# Revit family: LEGRAND_ECLAIRAGE_DE_SECURITE_KICKSPOT
name_source: partatom
category: Luminaires
units: mm (PartAtom-declared; Revit-internal decimal feet)

## family parameters
Cote de connecteur circulaire = Utiliser le diamètre
Couper avec des vides une fois chargée = Non
Hôte = Face
Partagée = Non
Point de calcul de pièce = Non
Source d'éclairage = Oui
Type d'élément = Normal

## types (14) — shared parameters
Angle de l'inclinaison = 60.00°
CLASSE_DE_PROTECTION = II
CLASSE_DE_PROTECTION_(IP) = IP40
COULEUR_DU_BOITIER = blanc
Condition Générale d'Utilisation = https://export.legrand.com
DIAMETRE_EXTERNE = 187
DISTANCE_DE_RECONNAISSANCE = 15
DUREE_DE_GARANTIE_BAES_COMPLET = 2
Elévation par défaut = 1219 mm
Emettre à partir de la longueur de la ligne = 610 mm
FORMAT_PRODUIT = rond
Fichier de distribution photométrique = generic
Filtre de couleur = 16777215
Gradation des changements de température de couleur de lampe = <Aucun>
INSTALLATION_DE_SURVEILLANCE = auto-test automatique
LARGEUR = 187
MATERIAU_DU_BOITIER = plastique
MATERIAU_DU_COUVERCLE = plastique transparent
PROFONDEUR_D'ENCASTREMENT = 61.5
SOURCE_LUMINEUSE = LED non interchangeable
SUPPORT_PLAFOND = Oui
TYPE_DE_MONTAGE = encastré

## per-type parameters (varying)
| type | ADAPTE_AU_TYPE_DE_MARQUAGE | ALIMENTATION | CATEGORIE_PRODUIT | DIAMETRE_D'ENCASTREMENT | ETAT_DES_ACCUS | FLUX_LUMINEUX_EN_MODE_D'URGENCE | FONCTION | HAUTEUR/PROFONDEUR | LARGEUR_DE_MONTAGE | LONGUEUR | LONGUEUR_D'ENCASTREMENT | PORTE_PICTO | PUISSANCE_DE_LA_LAMPE | REFERENCE_ARTICLE | REF_BATTERIE_DE_RECHANGE | RESERVE_DE_MARCHE | TENSION_NOMINALE_(MAX) | TENSION_NOMINALE_(MIN) | TYPE_DE_COMMUTATION | TYPE_DE_TENSION |
| BAES+BAEH  KICKSPOT ECO1 AUTOD | feuillet/plaque inséré(e) | décentralisé (batterie individuelle) | Autonome | 152 | NiCd | 45 | BAEH | 202 | 152 | 240 | 152 | Oui | 1 | 062514 | 061087 | 1 | 253 | 207 | mode veille | CA |
| BAES EVAC KICKSPOT ECO1 AUTOD | feuillet/plaque inséré(e) | décentralisé (batterie individuelle) | Autonome | 152 | NiCd | 45 | Evac | 202 | 152 | 240 | 152 | Oui | 0.5 | 062524 | 061087 | 1 | 253 | 207 | mode veille | CA |
| DBR KICKSPOT ECO1 AUTOD | feuillet/plaque inséré(e) | décentralisé (batterie individuelle) | Autonome | 151 | NiCd | 45 | DBR | 202 | 151 | 240 | 151 | Oui | 1 | 062554 | 061087 | 1 | 253 | 207 | mode veille | CA |
| BAES AMB KICKSPOT ECO1 AUTOD |  | décentralisé (batterie individuelle) | Autonome | 152 | NiMh | 320 | Amb | 76 | 152 | 187 | 152 | Non | 4 | 062564 | 061088 | 1 | 253 | 207 | mode veille | CA |
| BAEH KICKSPOT ECO1 AUTOD | feuillet/plaque inséré(e) | décentralisé (batterie individuelle) | Autonome | 152 | NiCd | 8 | BAES+BAEH | 76 | 152 | 187 | 152 | Non | 0.09 | 062574 | 061087 | 5 | 253 | 207 | mode veille | CA |
| BAES+BAEH KICKSPOT ECO2 ADR | feuillet/plaque inséré(e) | décentralisé (batterie individuelle) | Autonome | 152 | NiMh | 45 | BAEH | 202 | 152 | 240 | 152 | Oui | 1 | 062614 | 2*061088 | 1 | 253 | 207 | mode veille | CA |
| BAES EVAC KICKSPOT ECO2 ADR | feuillet/plaque inséré(e) | décentralisé (batterie individuelle) | Autonome | 152 | NiMh | 45 | Evac | 202 | 152 | 240 | 152 | Oui | 0.5 | 062624 | 061088 | 1 | 253 | 207 | mode veille | CA |
| DBR KICKSPOT ECO2 ADR | feuillet/plaque inséré(e) | décentralisé (batterie individuelle) | Autonome | 152 | NiMh | 45 | DBR | 202 | 152 | 240 | 152 | Oui | 1 | 062654 | 061089 | 1 | 253 | 207 | mode veille | CA |
| BAES AMB KICKSPOT ECO2 ADR |  | décentralisé (batterie individuelle) | Autonome | 152 | NiMh | 320 | Amb | 76 | 152 | 187 | 152 | Non | 4 | 062664 | 061088 | 1 | 253 | 207 | mode veille | CA |
| BAEH KICKSPOT ECO2 ADR | feuillet/plaque inséré(e) | décentralisé (batterie individuelle) | Autonome | 152 | NiMh | 8 | BAES+BAEH | 76 | 152 | 187 | 152 | Non | 0.35 | 062674 | 061089 | 5 | 253 | 207 | mode veille | CA |
| LSC  KICKSPOT EVAC 24/48V | feuillet/plaque inséré(e) | central (batterie centrale) | LSC | 152 | non applicable | 45 | Evac | 202 | 152 | 240 | 152 | Oui | 1 | 062824 |  |  | 48 | 24 | circuit permanent/circuit de secours | CC |
| LSC AMB KICKSPOT 24/48V |  | central (batterie centrale) | LSC | 152 | non applicable | 320 | Amb | 76 | 152 | 187 | 152 | Non | 4 | 062864 |  |  | 48 | 24 | circuit permanent/circuit de secours | CC |
| LSC EVAC KICKSPOT 110/220V | feuillet/plaque inséré(e) | central (batterie centrale) | LSC | 152 | non applicable | 45 | Evac | 202 | 152 | 240 | 152 | Oui | 1 | 062924 |  |  | 220 | 110 | circuit permanent/circuit de secours | CC |
| LSC AMB  KICKSPOT 110/220V |  | central (batterie centrale) | LSC | 152 | non applicable | 320 | Amb | 76 | 152 | 187 | 152 | Non | 4 | 062964 |  |  | 220 | 110 | circuit permanent/circuit de secours | CC |

note: column(s) folded — value = type name in every type: DESIGNATION_ARTICLE
